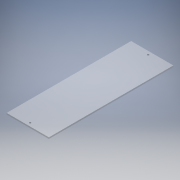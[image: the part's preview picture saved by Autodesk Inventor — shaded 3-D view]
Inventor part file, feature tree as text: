
AUTODESK INVENTOR PART (.ipt)
format: ipt  version: 2018 (Build 220112000, 112)  size: 123,392 bytes
history: native  units: mm
features: extrude x2, sketch x2
ambient origin geometry x8: Origin, YZ Plane, XZ Plane, XY Plane, X Axis, Y Axis, Z Axis, Center Point
bodies: Volumenkörper1 (feature_tree)
feature tree (4):
  extrude  "Extrusion1"  Depth=180.0mm
  extrude  "Extrusion3"  Depth=10.0mm
  sketch  "Skizze1"  dims[d0=529.8mm d1=180.0mm]
  sketch  "Sketch4"  dims[d2=6.0mm d3=0.0mm d11=7.65mm d12=93.75mm d13=14.0mm d14=7.65mm d15=14.0mm d16=93.75mm d17=10.0mm d18=0.0mm]
